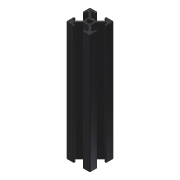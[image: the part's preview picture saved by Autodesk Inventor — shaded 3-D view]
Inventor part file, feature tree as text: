
AUTODESK INVENTOR PART (.ipt)
format: ipt  version: 2014 (Build 180170000, 170)  size: 377,856 bytes
history: native  units: mm
features: other x20, fillet x3, extrude x2, sketch x2, pattern_circular x1
ambient origin geometry x8: Origin, YZ Plane, XZ Plane, XY Plane, X Axis, Y Axis, Z Axis, Center Point
bodies: Solid1 (feature_tree)
feature tree (28):
  other  "Table"
  other  "Length = 50 mm"
  other  "Length = 75"
  other  "Length = 100"
  other  "Length = 150 mm"
  other  "Length = 125 mm"
  other  "Length = 175 mm"
  other  "Length = 200 mm"
  other  "Length = 250 mm"
  other  "Length = 225 mm"
  other  "Length = 300 mm"
  other  "Length = 325 mm"
  other  "Length = 350 mm"
  other  "Length = 400 mm"
  other  "Length = 375 mm"
  other  "Length = 450 mm"
  other  "Length = 425 mm"
  other  "Length = 475 mm"
  other  "Length = 500 mm"
  other  "Length = 275 mm"
  extrude  "Extrusion1"  Depth=8.76mm
  extrude  "Extrusion2"  Depth=0.75mm
  pattern_circular  "Circular Pattern1"  [2 undecoded]
  fillet  "Fillet9"  Radius=8.1mm
  fillet  "Fillet10"  Radius=2.14mm
  fillet  "Fillet11"  Radius=200.0mm
  sketch  "Sketch1"  dims[d0=8.76mm d1=5.0mm]
  sketch  "Sketch2"  dims[d3=0.0mm d4=12.5mm d5=2.14mm d6=8.1mm d7=2.14mm d8=200.0mm d9=0.0mm d10=40.0mm d11=360.0deg d23=1.0mm d24=0.75mm d25=0.75mm]
note: 2 required parameter values undecoded (feature->parameter linkage not recoverable at this tier; creation-order binding heuristic only, values carry confidence <= 0.55)
